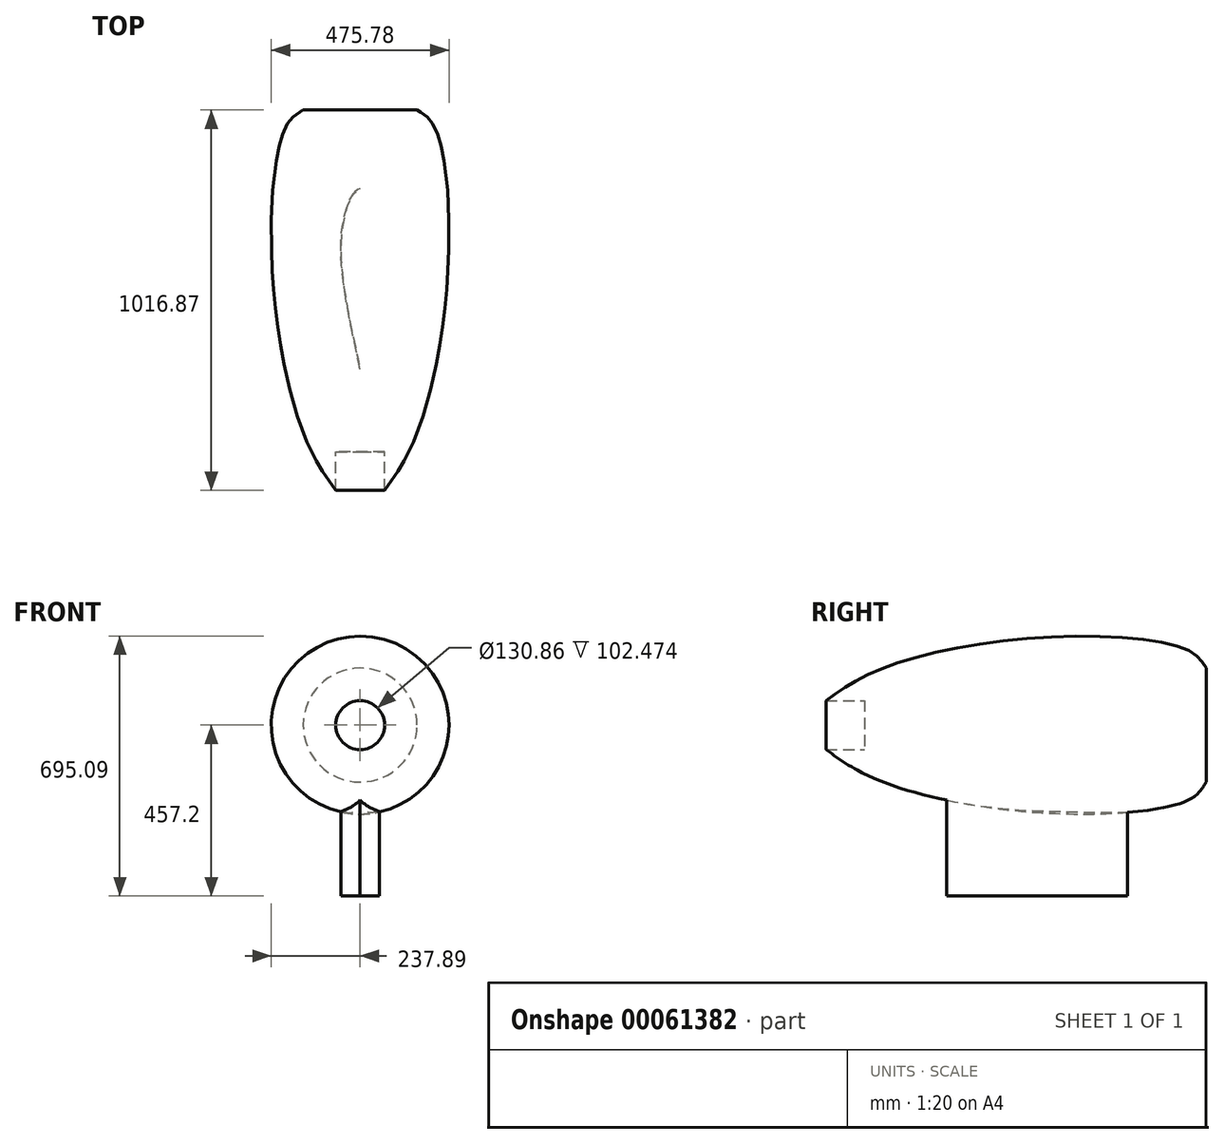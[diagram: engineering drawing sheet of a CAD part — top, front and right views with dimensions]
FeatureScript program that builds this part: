
annotation { "Feature Type Name" : "Feature", "Feature Type Description" : "" }
export const myFeature = defineFeature(function(context is Context, id is Id, definition is map)
    precondition{}
    {
        {
            var Q0;
            Q0=qCreatedBy(makeId("Right.planeOp"),FACE);
            var sketch = newSketch(context, id + "F0", { "sketchPlane" : qUnion([Q0])});
            skLineSegment(sketch, "E0", {"start": v(0, 0) * mm, "end": v(-914.4, 0) * mm});
            skLineSegment(sketch, "E1", {"start": v(0, 0) * mm, "end": v(0, 152.4) * mm});
            skFitSpline(sketch, "E2", {"points": [v(0, 152.4) * mm, v(-47.34, 200.25) * mm, v(-445.17, 234.14) * mm, v(-880.58, 145.73) * mm, v(-1016.87, 65.43) * mm], "startDerivative": vector(-226.44, 388.1) * mm, "endDerivative": vector(-560.9, -406.85) * mm});
            skLineSegment(sketch, "E3", {"start": v(-914.4, 0) * mm, "end": v(-914.4, 65.43) * mm});
            skLineSegment(sketch, "E4", {"start": v(-1016.87, 65.43) * mm, "end": v(-914.4, 65.43) * mm});
            skSolve(sketch);
        }
        {
            var Q0;
            Q0 = qSketchRegion(id + "F0", true);
            var Q1;
            Q1=sQuery(id+"F0.wireOp",EDGE,"E0");
            revolve(context, id + "F1", {"entities" : qUnion([Q0]), "axis" : qUnion([Q1]), "revolveType" : RevolveType.FULL});
        }
        {
            var Q0;
            Q0=qCreatedBy(makeId("Top.planeOp"),FACE);
            cPlane(context, id + "F2", {"entities" : qUnion([Q0]), "cplaneType" : CPlaneType.OFFSET, "offset" : 457.2 * mm, "oppositeDirection" : true, "width" : 152.4 * mm, "height" : 152.4 * mm});
        }
        {
            var Q0;
            Q0=qCreatedBy(id+"F2.planeOp",FACE);
            var sketch = newSketch(context, id + "F3", { "sketchPlane" : qUnion([Q0])});
            skLineSegment(sketch, "E5", {"start": v(0, 0) * mm, "end": v(0, -964.01) * mm});
            skFitSpline(sketch, "E6", {"points": [v(0, -209.84) * mm, v(-48.77, -320.6) * mm, v(0, -693.62) * mm], "startDerivative": vector(-169.28, -22.5) * mm, "endDerivative": vector(143.8, -673.45) * mm});
            skFitSpline(sketch, "E7.MirrorCS", {"points": [v(0, -209.84) * mm, v(48.77, -320.6) * mm, v(0, -693.62) * mm], "startDerivative": vector(169.28, -22.5) * mm, "endDerivative": vector(-143.8, -673.45) * mm});
            skSolve(sketch);
        }
        {
            var Q0;
            Q0 = qSketchRegion(id + "F3", true);
            extrude(context, id + "F4", {"entities" : qUnion([Q0]), "endBound" : BoundingType.UP_TO_NEXT, "depth" : 25.4 * mm});
        }
    });
